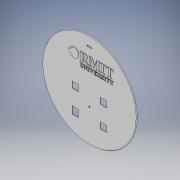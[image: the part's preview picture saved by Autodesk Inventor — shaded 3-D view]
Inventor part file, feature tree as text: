
AUTODESK INVENTOR PART (.ipt)
format: ipt  version: 2018 (Build 220112000, 112)  size: 1,027,072 bytes
history: native  units: in
note: dims shown in document units (in); Inventor stores cm internally (conversion verified against a paired STEP export)
features: extrude x7, fillet x3, sketch x2, emboss x1, other x1
ambient origin geometry x8: Origin, YZ Plane, XZ Plane, XY Plane, X Axis, Y Axis, Z Axis, Center Point
bodies: Solid1 (feature_tree)
feature tree (14):
  extrude  "Extrusion2"  Depth=1.0236in
  extrude  "Extrusion3"  Depth=0.0394in
  fillet  "Fillet1"  Radius=1.0236in
  fillet  "Fillet2"  Radius=1.0236in
  extrude  "Extrusion4"  Depth=0.0394in
  extrude  "Extrusion5"  Depth=0.1181in
  extrude  "Extrusion7"  Depth=0.0394in TaperAngle=0.0deg
  extrude  "Extrusion8"  Depth=0.0394in TaperAngle=0.0deg
  fillet  "Fillet4"  Radius=0.0984in
  emboss  "Emboss2"
  extrude  "Extrusion9"  Depth=0.0394in
  other  "Image1"
  sketch  "Sketch1"  dims[d118=1.0236in d119=1.0236in]
  sketch  "Sketch2"  dims[d122=1.0236in d123=1.0236in d124=1.0236in d125=1.0236in d126=15.2953in d127=0.1181in d130=0.2165in d131=0.0in d132=0.0984in d133=0.0in d134=0.0984in d135=0.0394in d145=0.7874in d146=0.1969in d148=0.0984in d149=0.0in d150=0.0394in d151=0.0in d154=15.748in d155=13.7795in d156=15.3543in d157=1.9685in d158=4.4882in d159=1.9685in d160=7.874in d161=3.7795in d162=3.7795in d163=1.6811in d164=2.3622in d165=1.5748in d166=1.5748in d167=2.2835in d168=4.3307in d169=4.3307in d170=1.437in d171=2.6181in d172=1.6811in d173=0.4724in d174=0.4724in d175=2.0472in d176=2.2638in d177=4.4882in d178=0.5906in d179=0.1181in d180=0.1181in d181=0.7087in d182=0.5906in d183=0.1181in d184=0.7087in d185=1.9685in d186=0.3937in d187=0.7874in d188=1.9685in d189=0.3937in d190=0.7874in d191=0.3937in d192=0.1181in d193=0.3937in d194=0.1181in d195=0.1181in d196=0.7087in d197=0.1181in d198=0.5906in d199=0.3937in d200=0.1181in d201=0.1181in d202=0.7087in d203=0.3937in d204=0.1181in d205=0.1181in d206=0.7087in d207=1.0748in d208=1.0748in d209=0.1969in d210=0.1969in d211=0.1969in d212=0.1969in d213=0.2362in d214=0.4724in d215=0.1575in d216=0.2362in d217=0.1575in d218=360.0deg d219=0.1181in d220=3.1496in d221=0.1969in d222=1.8504in d223=5.9843in d224=3.7402in d225=0.1969in d226=0.1969in d227=0.1969in d228=1.1811in d229=2.3622in d230=0.6693in d231=1.0236in d232=0.5118in d233=0.5118in d234=0.1969in d235=0.1969in d236=1.0236in d237=0.5118in d238=1.0236in d239=0.1969in d240=0.1969in d241=0.1969in d242=0.1969in d243=0.1969in d244=0.1969in d245=0.7874in d246=1.5748in d247=0.7874in d248=1.5748in d249=0.5906in d250=4.7244in d251=0.9843in d252=0.9843in d253=0.9843in d254=0.9843in d255=0.9843in d256=0.9843in d257=0.9843in d258=2.2323in d259=0.5906in d260=0.1181in d261=0.5906in d262=0.1181in d263=0.1181in d264=0.7087in d265=0.5906in d266=0.7087in d267=0.1181in d268=0.5906in d269=0.1181in d270=8.2677in d287=1.0236in d288=1.0236in d289=1.0236in d290=0.1969in d291=0.0984in d292=0.0in d293=0.0984in d294=0.0in d295=0.0394in d296=0.0394in d297=0.0in d298=0.0787in d300=0.0787in d301=0.0394in d302=0.0in]
